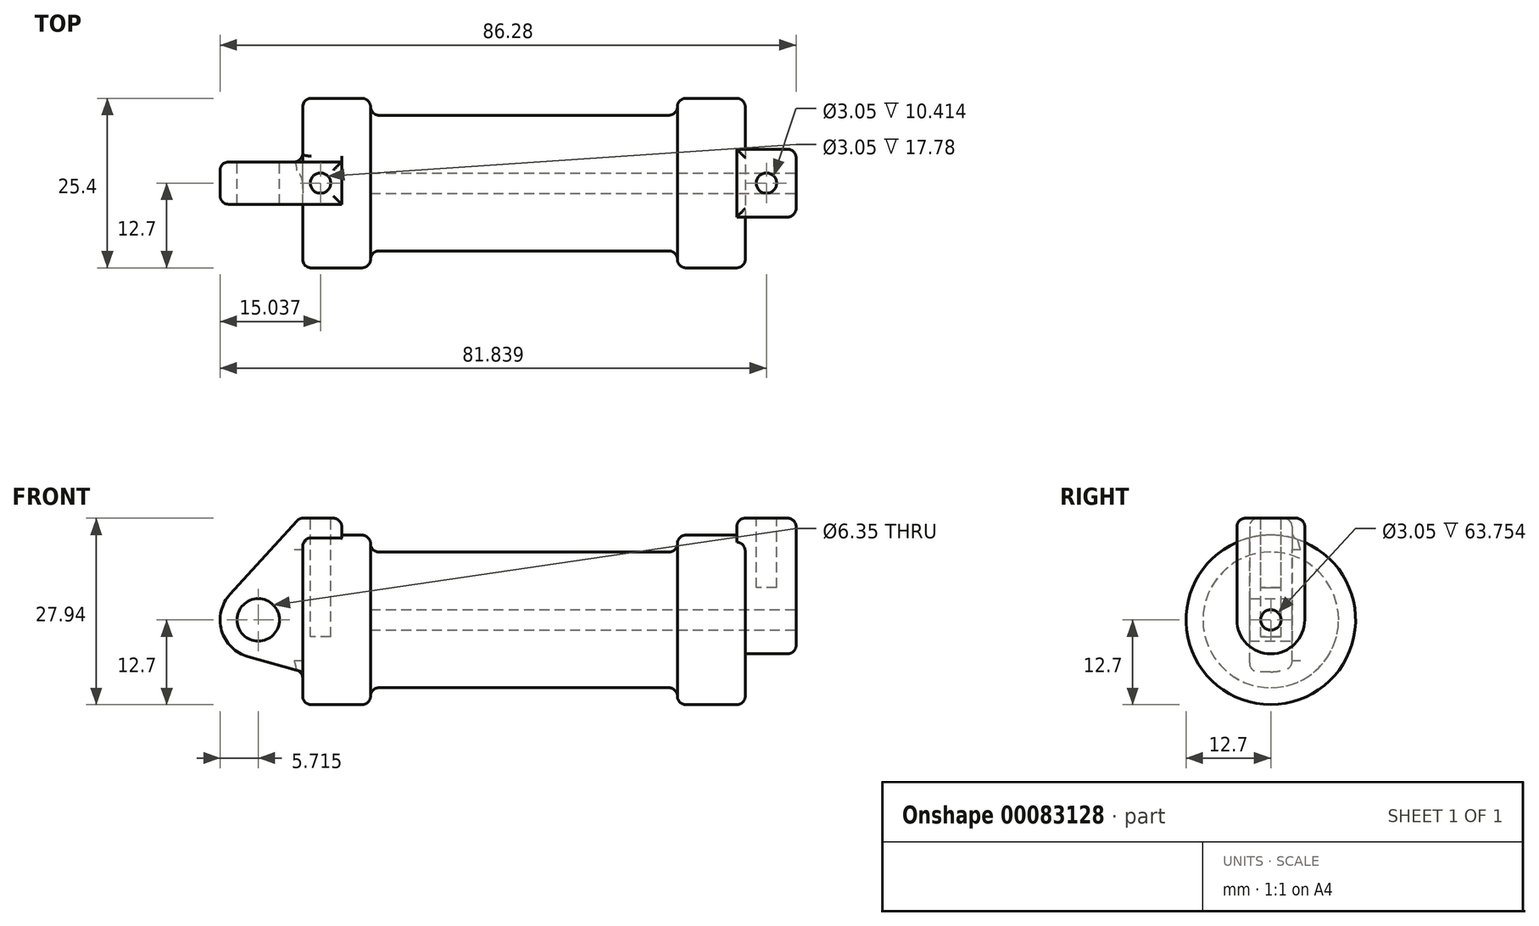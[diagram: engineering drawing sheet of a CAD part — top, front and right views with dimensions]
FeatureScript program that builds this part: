
annotation { "Feature Type Name" : "Feature", "Feature Type Description" : "" }
export const myFeature = defineFeature(function(context is Context, id is Id, definition is map)
    precondition{}
    {
        {
            var Q0;
            Q0=qCreatedBy(makeId("Front.planeOp"),FACE);
            var sketch = newSketch(context, id + "F0", { "sketchPlane" : qUnion([Q0])});
            skLineSegment(sketch, "E0", {"start": v(0, 0) * mm, "end": v(0, 12.7) * mm});
            skLineSegment(sketch, "E1", {"start": v(0, 12.7) * mm, "end": v(10.16, 12.7) * mm});
            skLineSegment(sketch, "E2", {"start": v(10.16, 12.7) * mm, "end": v(10.16, 10.16) * mm});
            skLineSegment(sketch, "E3", {"start": v(10.16, 10.16) * mm, "end": v(56.13, 10.16) * mm});
            skLineSegment(sketch, "E4", {"start": v(56.13, 10.16) * mm, "end": v(56.13, 12.7) * mm});
            skLineSegment(sketch, "E5", {"start": v(56.13, 12.7) * mm, "end": v(66.3, 12.7) * mm});
            skLineSegment(sketch, "E6", {"start": v(66.3, 12.7) * mm, "end": v(66.3, 0) * mm});
            skLineSegment(sketch, "E7", {"start": v(66.3, 0) * mm, "end": v(0, 0) * mm});
            skLineSegment(sketch, "E8", {"start": v(5.84, 15.24) * mm, "end": v(-0.5, 15.24) * mm});
            skLineSegment(sketch, "E9", {"start": v(-0.5, 15.24) * mm, "end": v(-10.88, 3.85) * mm});
            skLineSegment(sketch, "E10", {"start": v(0, 0) * mm, "end": v(-6.65, 0) * mm});
            skCircle(sketch, "E11", {"center": v(-6.65, 0) * mm, "radius": 5.72 * mm});
            skCircle(sketch, "E12", {"center": v(-6.65, 0) * mm, "radius": 3.18 * mm});
            skLineSegment(sketch, "E13", {"start": v(5.84, 15.24) * mm, "end": v(5.84, -9.4) * mm});
            skLineSegment(sketch, "E14", {"start": v(5.84, -9.4) * mm, "end": v(-8.18, -5.5) * mm});
            skSolve(sketch);
        }
        {
            var Q0;
            {var subQ3=sQuery(id+"F0.wireOp",EDGE,"E0");Q0=makeQuery(id+"F0.imprint","IMPRINT",FACE,{"disambiguationData":[TD([[makeQuery(id+"F0.imprint","IMPRINT",EDGE,{"derivedFrom":subQ3}),1.0]])]});}
            var Q1;
            {var subQ0=sQuery(id+"F0.wireOp",EDGE,"E0");Q1=makeQuery(id+"F0.imprint","IMPRINT",FACE,{"disambiguationData":[TD([[makeQuery(id+"F0.imprint","IMPRINT",EDGE,{"derivedFrom":subQ0}),-1.0]])]});}
            var Q2;
            {var subQ0=sQuery(id+"F0.wireOp",EDGE,"E14");Q2=makeQuery(id+"F0.imprint","IMPRINT",FACE,{"disambiguationData":[TD([[makeQuery(id+"F0.imprint","IMPRINT",EDGE,{"derivedFrom":subQ0}),-1.0]])]});}
            var Q3;
            {var subQ4=sQuery(id+"F0.wireOp",EDGE,"E12");Q3=makeQuery(id+"F0.imprint","IMPRINT",FACE,{"disambiguationData":[TD([[makeQuery(id+"F0.imprint","IMPRINT",EDGE,{"derivedFrom":subQ4}),-1.0]])]});}
            extrude(context, id + "F1", {"entities" : qUnion([Q0, Q1, Q2, Q3]), "endBound" : BoundingType.SYMMETRIC, "depth" : 6.35 * mm});
        }
        {
            var Q0;
            {var subQ0=sQuery(id+"F0.wireOp",EDGE,"E2");Q0=makeQuery(id+"F0.imprint","IMPRINT",FACE,{"disambiguationData":[TD([[makeQuery(id+"F0.imprint","IMPRINT",EDGE,{"derivedFrom":subQ0}),-1.0]])]});}
            var Q1;
            {var subQ0=sQuery(id+"F0.wireOp",EDGE,"E0");Q1=makeQuery(id+"F0.imprint","IMPRINT",FACE,{"disambiguationData":[TD([[makeQuery(id+"F0.imprint","IMPRINT",EDGE,{"derivedFrom":subQ0}),-1.0]])]});}
            var Q2;
            Q2=sQuery(id+"F0.wireOp",EDGE,"E7");
            revolve(context, id + "F2", {"operationType" : NewBodyOperationType.ADD, "entities" : qUnion([Q0, Q1]), "axis" : qUnion([Q2]), "revolveType" : RevolveType.FULL});
        }
        {
            var Q0;
            Q0=makeQuery(id+"F2.opRevolve","SWEPT_FACE",FACE,{"disambiguationData":[OSD([sQuery(id+"F0.wireOp",EDGE,"E6")])]});
            var sketch = newSketch(context, id + "F3", { "sketchPlane" : qUnion([Q0])});
            skCircle(sketch, "E15", {"center": v(0, 0) * mm, "radius": 5.08 * mm});
            skLineSegment(sketch, "E16", {"start": v(-5.08, 0) * mm, "end": v(-5.08, 15.24) * mm});
            skLineSegment(sketch, "E17", {"start": v(5.08, 0) * mm, "end": v(5.08, 15.24) * mm});
            skLineSegment(sketch, "E18", {"start": v(5.08, 15.24) * mm, "end": v(-5.08, 15.24) * mm});
            skCircle(sketch, "E19", {"center": v(0, 0) * mm, "radius": 1.52 * mm});
            skSolve(sketch);
        }
        {
            var Q0;
            Q0=makeQuery(id+"F3.imprint","IMPRINT",FACE,{"disambiguationData":[TD([[makeQuery(id+"F3.imprint","IMPRINT",EDGE,{"derivedFrom":sQuery(id+"F3.wireOp",EDGE,"E19")}),1.0]])]});
            var Q1;
            Q1=makeQuery(id+"F2.opRevolve","SWEPT_FACE",FACE,{"disambiguationData":[OSD([sQuery(id+"F0.wireOp",EDGE,"E2")])]});
            extrude(context, id + "F4", {"entities" : qUnion([Q0]), "operationType" : NewBodyOperationType.REMOVE, "endBound" : BoundingType.UP_TO_SURFACE, "oppositeDirection" : true, "endBoundEntityFace" : qUnion([Q1]), "depth" : 25.4 * mm});
        }
        {
            var Q0;
            Q0 = qSketchRegion(id + "F3", true);
            extrude(context, id + "F5", {"entities" : qUnion([Q0]), "operationType" : NewBodyOperationType.ADD, "oppositeDirection" : true, "depth" : 1.27 * mm});
        }
        {
            var Q0;
            Q0 = qSketchRegion(id + "F3", true);
            var Q1;
            {var subQ0=sQuery(id+"F3.wireOp",EDGE,"E16");var subQ1=sQuery(id+"F3.wireOp",EDGE,"E15");var subQ2=makeQuery(id+"F3.imprint","INTERSECT",VERTEX,{"derivedFrom":[subQ1,subQ0]});Q1=makeQuery(id+"F3.imprint","IMPRINT",FACE,{"disambiguationData":[TD([[makeQuery(id+"F3.imprint","IMPRINT",EDGE,{"disambiguationData":[TD([[subQ2,1.0]])],"derivedFrom":subQ1}),-1.0]])]});}
            extrude(context, id + "F6", {"entities" : qUnion([Q0, Q1]), "operationType" : NewBodyOperationType.ADD, "depth" : 7.62 * mm});
        }
        {
            var Q0;
            {var subQ0=sQuery(id+"F3.wireOp",EDGE,"E18");Q0=makeQuery(id+"F6.boolean.opBoolean","MERGE",FACE,{"derivedFrom":[makeQuery(id+"F5.opExtrude","SWEPT_FACE",FACE,{"disambiguationData":[OSD([subQ0])]}),makeQuery(id+"F6.opExtrude","SWEPT_FACE",FACE,{"disambiguationData":[OSD([subQ0])]})]});}
            var sketch = newSketch(context, id + "F7", { "sketchPlane" : qUnion([Q0])});
            skCircle(sketch, "E20", {"center": v(69.47, 0) * mm, "radius": 1.52 * mm});
            skPoint(sketch, "E20.centerSnap0", {"position": v(69.47, 5.08) * mm});
            skPoint(sketch, "E20.centerSnap1", {"position": v(65.02, 0) * mm});
            skSolve(sketch);
        }
        {
            var Q0;
            Q0=makeQuery(id+"F7.imprint","IMPRINT",FACE,{"disambiguationData":[TD([[makeQuery(id+"F7.imprint","IMPRINT",EDGE,{"derivedFrom":sQuery(id+"F7.wireOp",EDGE,"E20")}),1.0]])]});
            extrude(context, id + "F8", {"entities" : qUnion([Q0]), "operationType" : NewBodyOperationType.REMOVE, "oppositeDirection" : true, "depth" : 10.4 * mm});
        }
        {
            var Q0;
            Q0=makeQuery(id+"F1.opExtrude","SWEPT_FACE",FACE,{"disambiguationData":[OSD([sQuery(id+"F0.wireOp",EDGE,"E8")])]});
            var sketch = newSketch(context, id + "F9", { "sketchPlane" : qUnion([Q0])});
            skCircle(sketch, "E21", {"center": v(2.67, 0) * mm, "radius": 1.52 * mm});
            skPoint(sketch, "E21.centerSnap0", {"position": v(5.84, 0) * mm});
            skPoint(sketch, "E21.centerSnap1", {"position": v(2.67, -3.18) * mm});
            skSolve(sketch);
        }
        {
            var Q0;
            Q0=makeQuery(id+"F9.imprint","IMPRINT",FACE,{"disambiguationData":[TD([[makeQuery(id+"F9.imprint","IMPRINT",EDGE,{"derivedFrom":sQuery(id+"F9.wireOp",EDGE,"E21")}),1.0]])]});
            extrude(context, id + "F10", {"entities" : qUnion([Q0]), "operationType" : NewBodyOperationType.REMOVE, "oppositeDirection" : true, "depth" : 17.78 * mm});
        }
        {
            var Q0;
            Q0=makeQuery(id+"F2.opRevolve","SWEPT_EDGE",EDGE,{"disambiguationData":[OSD([sQuery(id+"F0.wireOp",EDGE,"E4"),sQuery(id+"F0.wireOp",EDGE,"E5")])]});
            var Q1;
            Q1=makeQuery(id+"F2.opRevolve","SWEPT_EDGE",EDGE,{"disambiguationData":[OSD([sQuery(id+"F0.wireOp",EDGE,"E5"),sQuery(id+"F0.wireOp",EDGE,"E6")])]});
            var Q2;
            Q2=makeQuery(id+"F2.opRevolve","SWEPT_EDGE",EDGE,{"disambiguationData":[OSD([sQuery(id+"F0.wireOp",EDGE,"E3"),sQuery(id+"F0.wireOp",EDGE,"E4")])]});
            var Q3;
            Q3=makeQuery(id+"F2.opRevolve","SWEPT_EDGE",EDGE,{"disambiguationData":[OSD([sQuery(id+"F0.wireOp",EDGE,"E0"),sQuery(id+"F0.wireOp",EDGE,"E1")])]});
            var Q4;
            Q4=makeQuery(id+"F2.opRevolve","SWEPT_EDGE",EDGE,{"disambiguationData":[OSD([sQuery(id+"F0.wireOp",EDGE,"E1"),sQuery(id+"F0.wireOp",EDGE,"E2")])]});
            var Q5;
            Q5=makeQuery(id+"F2.opRevolve","SWEPT_EDGE",EDGE,{"disambiguationData":[OSD([sQuery(id+"F0.wireOp",EDGE,"E2"),sQuery(id+"F0.wireOp",EDGE,"E3")])]});
            fillet(context, id + "F11", {"entities" : qUnion([Q0, Q1, Q2, Q3, Q4, Q5]), "radius" : 1.27 * mm, "tangentPropagation" : true, "allowEdgeOverflow" : false});
        }
        {
            var Q0;
            Q0=makeQuery(id+"F1.opExtrude","CAP_EDGE",EDGE,{"disambiguationData":[OSD([sQuery(id+"F0.wireOp",EDGE,"E9")])],"isStart":false});
            var Q1;
            Q1=makeQuery(id+"F1.opExtrude","CAP_EDGE",EDGE,{"disambiguationData":[OSD([sQuery(id+"F0.wireOp",EDGE,"E14")])],"isStart":true});
            var Q2;
            Q2=makeQuery(id+"F2.boolean.opBoolean","INTERSECT",EDGE,{"derivedFrom":[makeQuery(id+"F1.opExtrude","CAP_FACE",FACE,{"disambiguationData":[OSD([sQuery(id+"F0.wireOp",EDGE,"E8"),sQuery(id+"F0.wireOp",EDGE,"E9"),sQuery(id+"F0.wireOp",EDGE,"E11"),sQuery(id+"F0.wireOp",EDGE,"E12"),sQuery(id+"F0.wireOp",EDGE,"E13"),sQuery(id+"F0.wireOp",EDGE,"E14")])],"isStart":true}),makeQuery(id+"F2.opRevolve","SWEPT_FACE",FACE,{"disambiguationData":[OSD([sQuery(id+"F0.wireOp",EDGE,"E0")])]})]});
            var Q3;
            Q3=makeQuery(id+"F1.opExtrude","CAP_EDGE",EDGE,{"disambiguationData":[OSD([sQuery(id+"F0.wireOp",EDGE,"E8")])],"isStart":false});
            var Q4;
            Q4=makeQuery(id+"F1.opExtrude","CAP_EDGE",EDGE,{"disambiguationData":[OSD([sQuery(id+"F0.wireOp",EDGE,"E8")])],"isStart":true});
            var Q5;
            Q5=makeQuery(id+"F1.opExtrude","SWEPT_EDGE",EDGE,{"disambiguationData":[OSD([sQuery(id+"F0.wireOp",EDGE,"E8"),sQuery(id+"F0.wireOp",EDGE,"E13")])]});
            var Q6;
            Q6=makeQuery(id+"F1.opExtrude","SWEPT_EDGE",EDGE,{"disambiguationData":[OSD([sQuery(id+"F0.wireOp",EDGE,"E8"),sQuery(id+"F0.wireOp",EDGE,"E9")])]});
            fillet(context, id + "F12", {"entities" : qUnion([Q0, Q1, Q2, Q3, Q4, Q5, Q6]), "radius" : 1.27 * mm, "tangentPropagation" : true, "allowEdgeOverflow" : false});
        }
        {
            var Q0;
            Q0=makeQuery(id+"F6.opExtrude","CAP_EDGE",EDGE,{"disambiguationData":[OSD([sQuery(id+"F3.wireOp",EDGE,"E16")])],"isStart":false});
            var Q1;
            {var subQ0=sQuery(id+"F3.wireOp",EDGE,"E18");var subQ1=sQuery(id+"F3.wireOp",EDGE,"E16");Q1=makeQuery(id+"F6.boolean.opBoolean","MERGE",EDGE,{"derivedFrom":[makeQuery(id+"F5.opExtrude","SWEPT_EDGE",EDGE,{"disambiguationData":[OSD([subQ1,subQ0])]}),makeQuery(id+"F6.opExtrude","SWEPT_EDGE",EDGE,{"disambiguationData":[OSD([subQ1,subQ0])]})]});}
            var Q2;
            Q2=makeQuery(id+"F5.opExtrude","CAP_EDGE",EDGE,{"disambiguationData":[OSD([sQuery(id+"F3.wireOp",EDGE,"E18")])],"isStart":false});
            var Q3;
            {var subQ0=sQuery(id+"F3.wireOp",EDGE,"E18");var subQ1=sQuery(id+"F3.wireOp",EDGE,"E17");Q3=makeQuery(id+"F6.boolean.opBoolean","MERGE",EDGE,{"derivedFrom":[makeQuery(id+"F5.opExtrude","SWEPT_EDGE",EDGE,{"disambiguationData":[OSD([subQ1,subQ0])]}),makeQuery(id+"F6.opExtrude","SWEPT_EDGE",EDGE,{"disambiguationData":[OSD([subQ1,subQ0])]})]});}
            var Q4;
            Q4=makeQuery(id+"F6.opExtrude","CAP_EDGE",EDGE,{"disambiguationData":[OSD([sQuery(id+"F3.wireOp",EDGE,"E18")])],"isStart":false});
            fillet(context, id + "F13", {"entities" : qUnion([Q0, Q1, Q2, Q3, Q4]), "radius" : 1.27 * mm, "tangentPropagation" : true, "allowEdgeOverflow" : false});
        }
    });
